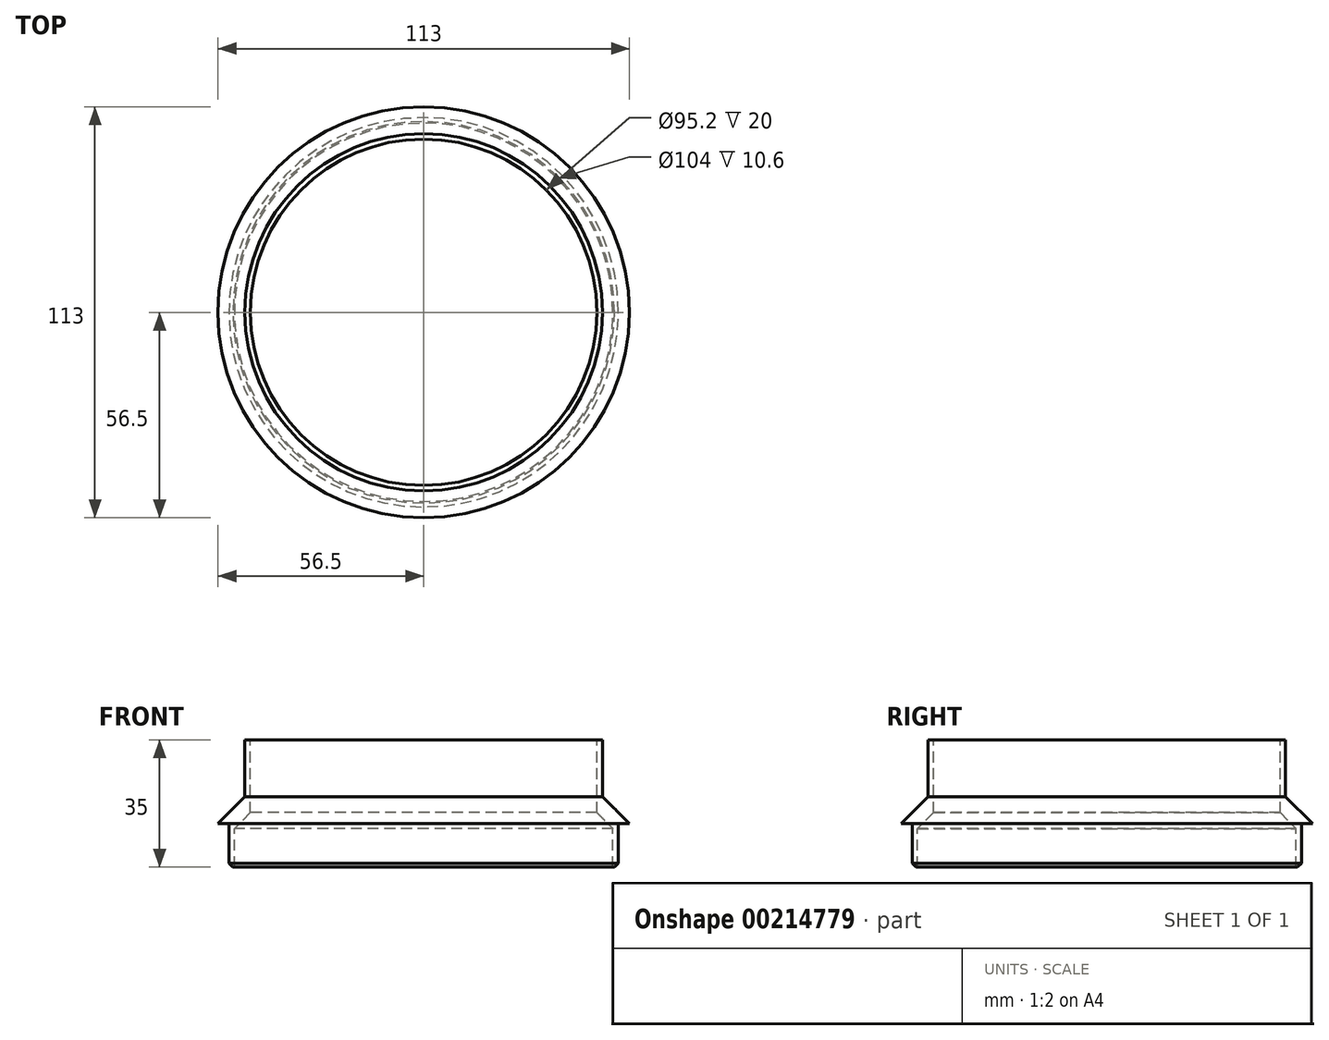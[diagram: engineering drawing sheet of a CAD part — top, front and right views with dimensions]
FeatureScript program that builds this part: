
annotation { "Feature Type Name" : "Feature", "Feature Type Description" : "" }
export const myFeature = defineFeature(function(context is Context, id is Id, definition is map)
    precondition{}
    {
        {
            var Q0;
            Q0=qCreatedBy(makeId("Front.planeOp"),FACE);
            var sketch = newSketch(context, id + "F0", { "sketchPlane" : qUnion([Q0])});
            skLineSegment(sketch, "E0", {"start": v(0, 55.93) * mm, "end": v(0, -56.28) * mm, "construction": true});
            skLineSegment(sketch, "E1.bottom", {"start": v(47.6, 20) * mm, "end": v(49.1, 20) * mm});
            skLineSegment(sketch, "E1.top", {"start": v(47.6, 0) * mm, "end": v(49.1, 0) * mm});
            skLineSegment(sketch, "E1.left", {"start": v(47.6, 20) * mm, "end": v(47.6, 0) * mm});
            skLineSegment(sketch, "E1.right", {"start": v(49.1, 20) * mm, "end": v(49.1, 0) * mm});
            skLineSegment(sketch, "E2.bottom", {"start": v(52, 0) * mm, "end": v(53.5, 0) * mm});
            skLineSegment(sketch, "E2.top", {"start": v(52, -15) * mm, "end": v(53.5, -15) * mm});
            skLineSegment(sketch, "E2.left", {"start": v(52, 0) * mm, "end": v(52, -15) * mm});
            skLineSegment(sketch, "E2.right", {"start": v(53.5, 0) * mm, "end": v(53.5, -15) * mm});
            skLineSegment(sketch, "E3", {"start": v(47.6, 0) * mm, "end": v(52, -4.4) * mm});
            skLineSegment(sketch, "E4", {"start": v(49.1, 4.4) * mm, "end": v(53.5, 0) * mm});
            skLineSegment(sketch, "E5", {"start": v(53.5, 0) * mm, "end": v(56.5, -3) * mm});
            skLineSegment(sketch, "E6", {"start": v(56.5, -3) * mm, "end": v(53.5, -3) * mm});
            skSolve(sketch);
        }
        {
            var Q0;
            {var subQ1=sQuery(id+"F0.wireOp",EDGE,"E1.bottom");Q0=makeQuery(id+"F0.imprint","IMPRINT",FACE,{"disambiguationData":[TD([[makeQuery(id+"F0.imprint","IMPRINT",EDGE,{"derivedFrom":subQ1}),-1.0]])]});}
            var Q1;
            {var subQ0=sQuery(id+"F0.wireOp",EDGE,"E5");Q1=makeQuery(id+"F0.imprint","IMPRINT",FACE,{"disambiguationData":[TD([[makeQuery(id+"F0.imprint","IMPRINT",EDGE,{"derivedFrom":subQ0}),-1.0]])]});}
            var Q2;
            {var subQ5=sQuery(id+"F0.wireOp",EDGE,"E1.top");Q2=makeQuery(id+"F0.imprint","IMPRINT",FACE,{"disambiguationData":[TD([[makeQuery(id+"F0.imprint","IMPRINT",EDGE,{"derivedFrom":subQ5}),-1.0]])]});}
            var Q3;
            {var subQ3=sQuery(id+"F0.wireOp",EDGE,"E2.bottom");Q3=makeQuery(id+"F0.imprint","IMPRINT",FACE,{"disambiguationData":[TD([[makeQuery(id+"F0.imprint","IMPRINT",EDGE,{"derivedFrom":subQ3}),-1.0]])]});}
            var Q4;
            Q4=sQuery(id+"F0.wireOp",EDGE,"E0");
            revolve(context, id + "F1", {"entities" : qUnion([Q0, Q1, Q2, Q3]), "axis" : qUnion([Q4]), "revolveType" : RevolveType.FULL});
        }
        {
            var Q0;
            Q0=makeQuery(id+"F1.opRevolve","SWEPT_EDGE",EDGE,{"disambiguationData":[OSD([sQuery(id+"F0.wireOp",EDGE,"E2.top"),sQuery(id+"F0.wireOp",EDGE,"E2.right")])]});
            chamfer(context, id + "F2", {"entities" : qUnion([Q0]), "width" : 1.1 * mm, "tangentPropagation" : true});
        }
    });
